# Revit family: Faucet-Deck_Mount-Bath-KALLISTA-PINNA_PALETTA-P24903_1
name_source: partatom
category: Plumbing Fixtures
units: mm (PartAtom-declared; Revit-internal decimal feet)

## family parameters
Cut with Voids When Loaded = No
Host = Face
Maintain Annotation Orientation = No
OmniClass Number = 23.31.11.00
OmniClass Title = Faucets
Part Type = Normal
Room Calculation Point = No
Round Connector Dimension = Use Diameter
Shared = No

## types (6) — shared parameters
Assembly Code = D2010
CW Connection = Yes
Cold Water Inlet = Cold Water Inlet
Date Modified = 11/22/2022
Default Elevation = 36"
Description = DECK-MOUNT BATH FAUCET WITH DIVERTER
Drain Included = No
Flow Rate = 11 GPM
HW Connection = Yes
Handle Clearance = 3 5/16"
Height = 9 1/8"
Hot Water Inlet = Hot Water Inlet
Length = 6 15/16"
Manufacturer = Kallista Co.
Master Format 2014 = 22 41 39
Master Format 2014 Name = Residential Faucets, Supplies, and Trim
Material = Premium Metal Construction
Pressure = 45.00 psi
Product Documentation Link = https://resources.kohler.com
Product Name = PINNA PALETTA
Spout Reach = 6 15/16"
URL = https://www.kallista.com
Vent Connection = No
Waste Connection = No
Waste Water Outlet = Waste Water Outlet
WaterSense Certified = No

## per-type parameters (varying)
| type | ADA Compliant | Finish | Model | Product Page URL | Secondary Finish | Type |
| BAF, BAF-Brushed French Gold | Yes | Kallista-Metal-BAF-Brushed_French_Gold | P24903-BAF-BAF | https://www.kallista.com | Kallista-Metal-BAF-Brushed_French_Gold | 1 |
| ULB, ULB-Unlaquered Brass | No | Kallista-Metal-ULB-Unlaquered_Brass | P24903-ULB-ULB | https://www.kallista.com | Kallista-Metal-ULB-Unlaquered_Brass | 5 |
| SNW, SN-Polished Nickel | No | Kallista-Metal-SN-Polished_Nickel | P24903-SNW-SN | https://www.kallista.com | Kallista-Metal-SNW-Polished_Nickel | 4 |
| CPH, CP-Chrome | No | Kallista-Metal-CP-Chrome | P24903-CPH-CP | https://www.kallista.com | Kallista-Metal-CPH-Polished_Chrome | 3 |
| BAF, BN-Brushed Nickel | Yes | Kallista-Metal-BN-Brushed_Nickel | P24903-BAF-BN |  | Kallista-Metal-BAF-Brushed_French_Gold | 2 |
| BNW, BN-Brushed Nickel | No | Kallista-Metal-BN-Brushed_Nickel | P24903-BNW-BN |  | Kallista-Metal-BNW-Brushed_Nickel | 6 |

## geometry (parser evidence)
native form markers: Sweep x7
no freeform markers — native parametric forms only
